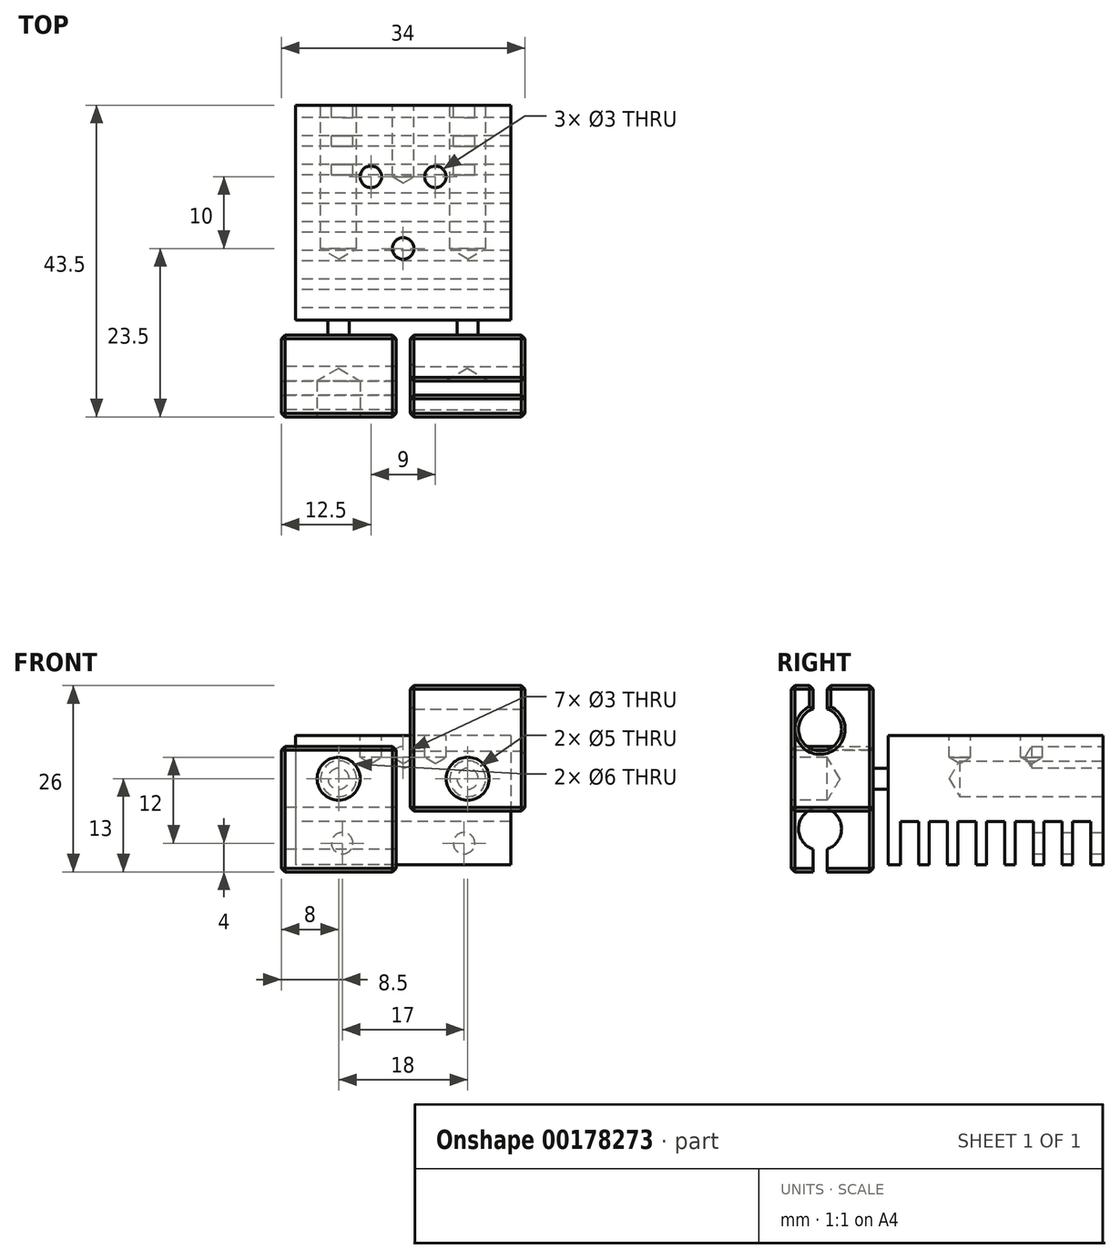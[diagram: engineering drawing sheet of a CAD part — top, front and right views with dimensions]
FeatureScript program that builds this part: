
annotation { "Feature Type Name" : "Feature", "Feature Type Description" : "" }
export const myFeature = defineFeature(function(context is Context, id is Id, definition is map)
    precondition{}
    {
        {
            var Q0;
            Q0=qCreatedBy(makeId("Top.planeOp"),FACE);
            var sketch = newSketch(context, id + "F0", { "sketchPlane" : qUnion([Q0])});
            skLineSegment(sketch, "E0.bottom", {"start": v(15, -15) * mm, "end": v(-15, -15) * mm});
            skLineSegment(sketch, "E0.top", {"start": v(15, 15) * mm, "end": v(-15, 15) * mm});
            skLineSegment(sketch, "E0.left", {"start": v(15, -15) * mm, "end": v(15, 15) * mm});
            skLineSegment(sketch, "E0.right", {"start": v(-15, -15) * mm, "end": v(-15, 15) * mm});
            skPoint(sketch, "E0.middle", {"position": v(0, 0) * mm});
            skSolve(sketch);
        }
        {
            var Q0;
            Q0=makeQuery(id+"F0.imprint","IMPRINT",FACE,{"disambiguationData":[TD([[makeQuery(id+"F0.imprint","IMPRINT",EDGE,{"derivedFrom":sQuery(id+"F0.wireOp",EDGE,"E0.bottom")}),-1.0]])]});
            extrude(context, id + "F10", {"entities" : qUnion([Q0]), "depth" : 18 * mm});
        }
        {
            var Q0;
            Q0=makeQuery(id+"F10.opExtrude","SWEPT_FACE",FACE,{"disambiguationData":[OSD([sQuery(id+"F0.wireOp",EDGE,"E0.top")])]});
            var sketch = newSketch(context, id + "F11", { "sketchPlane" : qUnion([Q0])});
            skPoint(sketch, "E1", {"position": v(-8.5, 3) * mm});
            skPoint(sketch, "E2", {"position": v(8.5, 3) * mm});
            skPoint(sketch, "E3", {"position": v(-9, 12) * mm});
            skPoint(sketch, "E4", {"position": v(9, 12) * mm});
            skPoint(sketch, "E5", {"position": v(0, 15) * mm});
            skSolve(sketch);
        }
        {
            var Q0;
            Q0=sQuery(id+"F11.wireOp",VERTEX,"E3");
            var Q1;
            Q1=sQuery(id+"F11.wireOp",VERTEX,"E4");
            var Q2;
            Q2=makeQuery(id+"F10.opExtrude","SWEPT_BODY",BODY,{"disambiguationData":[OSD([sQuery(id+"F0.wireOp",EDGE,"E0.bottom"),sQuery(id+"F0.wireOp",EDGE,"E0.top"),sQuery(id+"F0.wireOp",EDGE,"E0.left"),sQuery(id+"F0.wireOp",EDGE,"E0.right")])]});
            hole(context, id + "F1", {"style" : HoleStyle.SIMPLE, "endStyle" : HoleEndStyle.BLIND, "holeDiameter" : 5 * mm, "holeDepth" : 20 * mm, "locations" : qUnion([Q0, Q1]), "scope" : qUnion([Q2])});
        }
        {
            var Q0;
            Q0=makeQuery(id+"F10.opExtrude","CAP_FACE",FACE,{"disambiguationData":[OSD([sQuery(id+"F0.wireOp",EDGE,"E0.bottom"),sQuery(id+"F0.wireOp",EDGE,"E0.top"),sQuery(id+"F0.wireOp",EDGE,"E0.left"),sQuery(id+"F0.wireOp",EDGE,"E0.right")])],"isStart":true});
            var sketch = newSketch(context, id + "F12", { "sketchPlane" : qUnion([Q0])});
            skLineSegment(sketch, "E6.bottom", {"start": v(15, -13.25) * mm, "end": v(-15.01, -13.25) * mm});
            skLineSegment(sketch, "E6.top", {"start": v(15, -10.75) * mm, "end": v(-15.01, -10.75) * mm});
            skLineSegment(sketch, "E6.left", {"start": v(15, -13.25) * mm, "end": v(15, -10.75) * mm});
            skLineSegment(sketch, "E6.right", {"start": v(-15.01, -13.25) * mm, "end": v(-15.01, -10.75) * mm});
            skLineSegment(sketch, "E7.0.1.0", {"start": v(15, -9.25) * mm, "end": v(15, -6.75) * mm});
            skLineSegment(sketch, "E7.0.1.1", {"start": v(-15.01, -9.25) * mm, "end": v(-15.01, -6.75) * mm});
            skLineSegment(sketch, "E7.0.1.2", {"start": v(15, -9.25) * mm, "end": v(-15.01, -9.25) * mm});
            skLineSegment(sketch, "E7.0.1.3", {"start": v(15, -6.75) * mm, "end": v(-15.01, -6.75) * mm});
            skLineSegment(sketch, "E7.0.2.0", {"start": v(15, -5.25) * mm, "end": v(15, -2.75) * mm});
            skLineSegment(sketch, "E7.0.2.1", {"start": v(-15.01, -5.25) * mm, "end": v(-15.01, -2.75) * mm});
            skLineSegment(sketch, "E7.0.2.2", {"start": v(15, -5.25) * mm, "end": v(-15.01, -5.25) * mm});
            skLineSegment(sketch, "E7.0.2.3", {"start": v(15, -2.75) * mm, "end": v(-15.01, -2.75) * mm});
            skLineSegment(sketch, "E7.0.3.0", {"start": v(15, -1.25) * mm, "end": v(15, 1.25) * mm});
            skLineSegment(sketch, "E7.0.3.1", {"start": v(-15.01, -1.25) * mm, "end": v(-15.01, 1.25) * mm});
            skLineSegment(sketch, "E7.0.3.2", {"start": v(15, -1.25) * mm, "end": v(-15.01, -1.25) * mm});
            skLineSegment(sketch, "E7.0.3.3", {"start": v(15, 1.25) * mm, "end": v(-15.01, 1.25) * mm});
            skLineSegment(sketch, "E7.0.4.0", {"start": v(15, 2.75) * mm, "end": v(15, 5.25) * mm});
            skLineSegment(sketch, "E7.0.4.1", {"start": v(-15.01, 2.75) * mm, "end": v(-15.01, 5.25) * mm});
            skLineSegment(sketch, "E7.0.4.2", {"start": v(15, 2.75) * mm, "end": v(-15.01, 2.75) * mm});
            skLineSegment(sketch, "E7.0.4.3", {"start": v(15, 5.25) * mm, "end": v(-15.01, 5.25) * mm});
            skLineSegment(sketch, "E7.0.5.0", {"start": v(15, 6.75) * mm, "end": v(15, 9.25) * mm});
            skLineSegment(sketch, "E7.0.5.1", {"start": v(-15.01, 6.75) * mm, "end": v(-15.01, 9.25) * mm});
            skLineSegment(sketch, "E7.0.5.2", {"start": v(15, 6.75) * mm, "end": v(-15.01, 6.75) * mm});
            skLineSegment(sketch, "E7.0.5.3", {"start": v(15, 9.25) * mm, "end": v(-15.01, 9.25) * mm});
            skLineSegment(sketch, "E7.0.6.0", {"start": v(15, 10.75) * mm, "end": v(15, 13.25) * mm});
            skLineSegment(sketch, "E7.0.6.1", {"start": v(-15.01, 10.75) * mm, "end": v(-15.01, 13.25) * mm});
            skLineSegment(sketch, "E7.0.6.2", {"start": v(15, 10.75) * mm, "end": v(-15.01, 10.75) * mm});
            skLineSegment(sketch, "E7.0.6.3", {"start": v(15, 13.25) * mm, "end": v(-15.01, 13.25) * mm});
            skLineSegment(sketch, "E7.direction1", {"start": v(-15.01, -13.25) * mm, "end": v(9.99, -13.25) * mm, "construction": true});
            skLineSegment(sketch, "E7.direction2", {"start": v(-15.01, -13.25) * mm, "end": v(-15.01, -9.25) * mm, "construction": true});
            skSolve(sketch);
        }
        {
            var Q0;
            {var subQ0=sQuery(id+"F12.wireOp",EDGE,"E7.0.6.0");Q0=makeQuery(id+"F12.imprint","IMPRINT",FACE,{"disambiguationData":[TD([[makeQuery(id+"F12.imprint","IMPRINT",EDGE,{"derivedFrom":subQ0}),-1.0]])]});}
            var Q1;
            {var subQ0=sQuery(id+"F12.wireOp",EDGE,"E7.0.5.0");Q1=makeQuery(id+"F12.imprint","IMPRINT",FACE,{"disambiguationData":[TD([[makeQuery(id+"F12.imprint","IMPRINT",EDGE,{"derivedFrom":subQ0}),-1.0]])]});}
            var Q2;
            {var subQ0=sQuery(id+"F12.wireOp",EDGE,"E7.0.4.0");Q2=makeQuery(id+"F12.imprint","IMPRINT",FACE,{"disambiguationData":[TD([[makeQuery(id+"F12.imprint","IMPRINT",EDGE,{"derivedFrom":subQ0}),-1.0]])]});}
            var Q3;
            {var subQ0=sQuery(id+"F12.wireOp",EDGE,"E7.0.3.0");Q3=makeQuery(id+"F12.imprint","IMPRINT",FACE,{"disambiguationData":[TD([[makeQuery(id+"F12.imprint","IMPRINT",EDGE,{"derivedFrom":subQ0}),-1.0]])]});}
            var Q4;
            {var subQ0=sQuery(id+"F12.wireOp",EDGE,"E7.0.2.0");Q4=makeQuery(id+"F12.imprint","IMPRINT",FACE,{"disambiguationData":[TD([[makeQuery(id+"F12.imprint","IMPRINT",EDGE,{"derivedFrom":subQ0}),-1.0]])]});}
            var Q5;
            {var subQ0=sQuery(id+"F12.wireOp",EDGE,"E7.0.1.0");Q5=makeQuery(id+"F12.imprint","IMPRINT",FACE,{"disambiguationData":[TD([[makeQuery(id+"F12.imprint","IMPRINT",EDGE,{"derivedFrom":subQ0}),-1.0]])]});}
            var Q6;
            {var subQ0=sQuery(id+"F12.wireOp",EDGE,"E6.left");Q6=makeQuery(id+"F12.imprint","IMPRINT",FACE,{"disambiguationData":[TD([[makeQuery(id+"F12.imprint","IMPRINT",EDGE,{"derivedFrom":subQ0}),-1.0]])]});}
            extrude(context, id + "F13", {"entities" : qUnion([Q0, Q1, Q2, Q3, Q4, Q5, Q6]), "operationType" : NewBodyOperationType.REMOVE, "oppositeDirection" : true, "depth" : 6 * mm});
        }
        {
            var Q0;
            Q0=makeQuery(id+"F10.opExtrude","CAP_FACE",FACE,{"disambiguationData":[OSD([sQuery(id+"F0.wireOp",EDGE,"E0.bottom"),sQuery(id+"F0.wireOp",EDGE,"E0.top"),sQuery(id+"F0.wireOp",EDGE,"E0.left"),sQuery(id+"F0.wireOp",EDGE,"E0.right")])],"isStart":false});
            var sketch = newSketch(context, id + "F2", { "sketchPlane" : qUnion([Q0])});
            skPoint(sketch, "E8", {"position": v(-4.5, 5) * mm});
            skPoint(sketch, "E9", {"position": v(4.5, 5) * mm});
            skPoint(sketch, "E10", {"position": v(0, -5) * mm});
            skSolve(sketch);
        }
        {
            var Q0;
            Q0=sQuery(id+"F2.wireOp",VERTEX,"E9");
            var Q1;
            Q1=sQuery(id+"F2.wireOp",VERTEX,"E8");
            var Q2;
            Q2=sQuery(id+"F2.wireOp",VERTEX,"E10");
            var Q3;
            Q3=makeQuery(id+"F10.opExtrude","SWEPT_BODY",BODY,{"disambiguationData":[OSD([sQuery(id+"F0.wireOp",EDGE,"E0.bottom"),sQuery(id+"F0.wireOp",EDGE,"E0.top"),sQuery(id+"F0.wireOp",EDGE,"E0.left"),sQuery(id+"F0.wireOp",EDGE,"E0.right")])]});
            hole(context, id + "F14", {"style" : HoleStyle.SIMPLE, "endStyle" : HoleEndStyle.BLIND, "holeDiameter" : 3 * mm, "holeDepth" : 3 * mm, "locations" : qUnion([Q0, Q1, Q2]), "scope" : qUnion([Q3])});
        }
        {
            var Q0;
            Q0=sQuery(id+"F11.wireOp",VERTEX,"E2");
            var Q1;
            Q1=sQuery(id+"F11.wireOp",VERTEX,"E1");
            var Q2;
            Q2=sQuery(id+"F11.wireOp",VERTEX,"E5");
            var Q3;
            Q3=makeQuery(id+"F10.opExtrude","SWEPT_BODY",BODY,{"disambiguationData":[OSD([sQuery(id+"F0.wireOp",EDGE,"E0.bottom"),sQuery(id+"F0.wireOp",EDGE,"E0.top"),sQuery(id+"F0.wireOp",EDGE,"E0.left"),sQuery(id+"F0.wireOp",EDGE,"E0.right")])]});
            hole(context, id + "F15", {"style" : HoleStyle.SIMPLE, "endStyle" : HoleEndStyle.BLIND, "holeDiameter" : 3 * mm, "holeDepth" : 10 * mm, "locations" : qUnion([Q0, Q1, Q2]), "scope" : qUnion([Q3])});
        }
        {
            var Q0;
            Q0=makeQuery(id+"F10.opExtrude","SWEPT_FACE",FACE,{"disambiguationData":[OSD([sQuery(id+"F0.wireOp",EDGE,"E0.bottom")])]});
            var sketch = newSketch(context, id + "F3", { "sketchPlane" : qUnion([Q0])});
            skCircle(sketch, "E11", {"center": v(9, 12) * mm, "radius": 1.48 * mm});
            skCircle(sketch, "E12", {"center": v(-9, 12) * mm, "radius": 1.48 * mm});
            skSolve(sketch);
        }
        {
            var Q0;
            Q0=makeQuery(id+"F3.imprint","IMPRINT",FACE,{"disambiguationData":[TD([[makeQuery(id+"F3.imprint","IMPRINT",EDGE,{"derivedFrom":sQuery(id+"F3.wireOp",EDGE,"E12")}),1.0]])]});
            var Q1;
            Q1=makeQuery(id+"F3.imprint","IMPRINT",FACE,{"disambiguationData":[TD([[makeQuery(id+"F3.imprint","IMPRINT",EDGE,{"derivedFrom":sQuery(id+"F3.wireOp",EDGE,"E11")}),1.0]])]});
            extrude(context, id + "F4", {"entities" : qUnion([Q0, Q1]), "operationType" : NewBodyOperationType.ADD, "depth" : 2.1 * mm});
        }
        {
            var Q0;
            Q0=makeQuery(id+"F4.opExtrude","CAP_FACE",FACE,{"disambiguationData":[OSD([sQuery(id+"F3.wireOp",EDGE,"E11")])],"isStart":false});
            var sketch = newSketch(context, id + "F16", { "sketchPlane" : qUnion([Q0])});
            skLineSegment(sketch, "E13.bottom", {"start": v(1, 25) * mm, "end": v(17, 25) * mm});
            skLineSegment(sketch, "E13.top", {"start": v(1, 7.5) * mm, "end": v(17, 7.5) * mm});
            skLineSegment(sketch, "E13.left", {"start": v(1, 25) * mm, "end": v(1, 7.5) * mm});
            skLineSegment(sketch, "E13.right", {"start": v(17, 25) * mm, "end": v(17, 7.5) * mm});
            skPoint(sketch, "E14", {"position": v(9, 12) * mm});
            skSolve(sketch);
        }
        {
            var Q0;
            Q0=makeQuery(id+"F4.opExtrude","CAP_FACE",FACE,{"disambiguationData":[OSD([sQuery(id+"F3.wireOp",EDGE,"E12")])],"isStart":false});
            var sketch = newSketch(context, id + "F17", { "sketchPlane" : qUnion([Q0])});
            skPoint(sketch, "E15", {"position": v(-9, 12) * mm});
            skLineSegment(sketch, "E16.bottom", {"start": v(-17, 16.5) * mm, "end": v(-1, 16.5) * mm});
            skLineSegment(sketch, "E16.top", {"start": v(-17, -1) * mm, "end": v(-1, -1) * mm});
            skLineSegment(sketch, "E16.left", {"start": v(-17, 16.5) * mm, "end": v(-17, -1) * mm});
            skLineSegment(sketch, "E16.right", {"start": v(-1, 16.5) * mm, "end": v(-1, -1) * mm});
            skSolve(sketch);
        }
        {
            var Q0;
            Q0 = qSketchRegion(id + "F17", true);
            var Q1;
            Q1 = qSketchRegion(id + "F16", true);
            extrude(context, id + "F18", {"entities" : qUnion([Q0, Q1]), "operationType" : NewBodyOperationType.ADD, "depth" : 11.4 * mm});
        }
        {
            var Q0;
            Q0=makeQuery(id+"F18.opExtrude","CAP_FACE",FACE,{"disambiguationData":[OSD([sQuery(id+"F16.wireOp",EDGE,"E13.bottom"),sQuery(id+"F16.wireOp",EDGE,"E13.top"),sQuery(id+"F16.wireOp",EDGE,"E13.left"),sQuery(id+"F16.wireOp",EDGE,"E13.right")])],"isStart":false});
            var sketch = newSketch(context, id + "F19", { "sketchPlane" : qUnion([Q0])});
            skPoint(sketch, "E17", {"position": v(9, 12) * mm});
            skPoint(sketch, "E17.positionSnap0", {"position": v(9, 7.5) * mm});
            skSolve(sketch);
        }
        {
            var Q0;
            Q0=makeQuery(id+"F18.opExtrude","CAP_FACE",FACE,{"disambiguationData":[OSD([sQuery(id+"F17.wireOp",EDGE,"E16.bottom"),sQuery(id+"F17.wireOp",EDGE,"E16.top"),sQuery(id+"F17.wireOp",EDGE,"E16.left"),sQuery(id+"F17.wireOp",EDGE,"E16.right")])],"isStart":false});
            var sketch = newSketch(context, id + "F20", { "sketchPlane" : qUnion([Q0])});
            skPoint(sketch, "E18", {"position": v(-9, 12) * mm});
            skPoint(sketch, "E18.positionSnap0", {"position": v(-9, 16.5) * mm});
            skSolve(sketch);
        }
        {
            var Q0;
            Q0=sQuery(id+"F20.wireOp",VERTEX,"E18");
            var Q1;
            Q1=sQuery(id+"F19.wireOp",VERTEX,"E17");
            var Q2;
            Q2=makeQuery(id+"F10.opExtrude","SWEPT_BODY",BODY,{"disambiguationData":[OSD([sQuery(id+"F0.wireOp",EDGE,"E0.bottom"),sQuery(id+"F0.wireOp",EDGE,"E0.top"),sQuery(id+"F0.wireOp",EDGE,"E0.left"),sQuery(id+"F0.wireOp",EDGE,"E0.right")])]});
            hole(context, id + "F5", {"style" : HoleStyle.SIMPLE, "endStyle" : HoleEndStyle.BLIND, "holeDiameter" : 6 * mm, "holeDepth" : 5 * mm, "locations" : qUnion([Q0, Q1]), "scope" : qUnion([Q2])});
        }
        {
            var Q0;
            Q0=makeQuery(id+"F18.opExtrude","SWEPT_FACE",FACE,{"disambiguationData":[OSD([sQuery(id+"F16.wireOp",EDGE,"E13.right")])]});
            var sketch = newSketch(context, id + "F6", { "sketchPlane" : qUnion([Q0])});
            skArc(sketch, "E19", {"start": v(-25.5, 21.73) * mm, "mid": v(-24.5, 15.9) * mm, "end": v(-23.5, 21.73) * mm});
            skLineSegment(sketch, "E20.bottom", {"start": v(-25.5, 30.74) * mm, "end": v(-23.5, 30.74) * mm});
            skLineSegment(sketch, "E20.top", {"start": v(-25.5, 7.06) * mm, "end": v(-23.5, 7.06) * mm});
            skLineSegment(sketch, "E20.left", {"start": v(-25.5, 30.74) * mm, "end": v(-25.5, 21.73) * mm});
            skLineSegment(sketch, "E20.right", {"start": v(-23.5, 30.74) * mm, "end": v(-23.5, 21.73) * mm});
            skSolve(sketch);
        }
        {
            var Q0;
            {var subQ0=sQuery(id+"F6.wireOp",EDGE,"E19");Q0=makeQuery(id+"F6.imprint","IMPRINT",FACE,{"disambiguationData":[TD([[makeQuery(id+"F6.imprint","IMPRINT",EDGE,{"derivedFrom":subQ0}),1.0]])]});}
            extrude(context, id + "F7", {"entities" : qUnion([Q0]), "operationType" : NewBodyOperationType.REMOVE, "endBound" : BoundingType.UP_TO_NEXT, "oppositeDirection" : true, "depth" : 25 * mm});
        }
        {
            var Q0;
            Q0=makeQuery(id+"F18.opExtrude","SWEPT_FACE",FACE,{"disambiguationData":[OSD([sQuery(id+"F16.wireOp",EDGE,"E13.right")])]});
            var Q1;
            Q1=makeQuery(id+"F18.opExtrude","SWEPT_FACE",FACE,{"disambiguationData":[OSD([sQuery(id+"F16.wireOp",EDGE,"E13.top")])]});
            var Q2;
            Q2=makeQuery(id+"F18.opExtrude","SWEPT_FACE",FACE,{"disambiguationData":[OSD([sQuery(id+"F17.wireOp",EDGE,"E16.top")])]});
            var Q3;
            Q3=makeQuery(id+"F18.opExtrude","SWEPT_FACE",FACE,{"disambiguationData":[OSD([sQuery(id+"F17.wireOp",EDGE,"E16.right")])]});
            var Q4;
            {var subQ2=sQuery(id+"F16.wireOp",EDGE,"E13.bottom");Q4=makeQuery(id+"F7.boolean.opBoolean","SPLIT",FACE,{"disambiguationData":[TD([makeQuery(id+"F7.opExtrude","SWEPT_FACE",FACE,{"disambiguationData":[OSD([sQuery(id+"F6.wireOp",EDGE,"E20.right")])]})])],"derivedFrom":makeQuery(id+"F18.opExtrude","SWEPT_FACE",FACE,{"disambiguationData":[OSD([subQ2])]})});}
            var Q5;
            {var subQ2=sQuery(id+"F16.wireOp",EDGE,"E13.bottom");Q5=makeQuery(id+"F7.boolean.opBoolean","SPLIT",FACE,{"disambiguationData":[TD([makeQuery(id+"F7.opExtrude","SWEPT_FACE",FACE,{"disambiguationData":[OSD([sQuery(id+"F6.wireOp",EDGE,"E20.left")])]})])],"derivedFrom":makeQuery(id+"F18.opExtrude","SWEPT_FACE",FACE,{"disambiguationData":[OSD([subQ2])]})});}
            var Q6;
            Q6=makeQuery(id+"F18.opExtrude","SWEPT_FACE",FACE,{"disambiguationData":[OSD([sQuery(id+"F17.wireOp",EDGE,"E16.bottom")])]});
            var Q7;
            Q7=makeQuery(id+"F18.opExtrude","SWEPT_FACE",FACE,{"disambiguationData":[OSD([sQuery(id+"F17.wireOp",EDGE,"E16.left")])]});
            var Q8;
            Q8=makeQuery(id+"F18.opExtrude","SWEPT_FACE",FACE,{"disambiguationData":[OSD([sQuery(id+"F16.wireOp",EDGE,"E13.left")])]});
            chamfer(context, id + "F8", {"entities" : qUnion([Q0, Q1, Q2, Q3, Q4, Q5, Q6, Q7, Q8]), "width" : 0.5 * mm, "tangentPropagation" : true});
        }
        {
            var Q0;
            Q0=makeQuery(id+"F18.opExtrude","SWEPT_FACE",FACE,{"disambiguationData":[OSD([sQuery(id+"F17.wireOp",EDGE,"E16.left")])]});
            var sketch = newSketch(context, id + "F9", { "sketchPlane" : qUnion([Q0])});
            skArc(sketch, "E21", {"start": v(25.5, 2.17) * mm, "mid": v(24.5, 8) * mm, "end": v(23.5, 2.17) * mm});
            skLineSegment(sketch, "E22.top", {"start": v(25.5, -1.5) * mm, "end": v(23.5, -1.5) * mm});
            skLineSegment(sketch, "E22.left", {"start": v(25.5, 11.5) * mm, "end": v(25.5, 7.83) * mm});
            skLineSegment(sketch, "E22.right", {"start": v(23.5, 2.17) * mm, "end": v(23.5, -1.5) * mm});
            skPoint(sketch, "E23.orphan", {"position": v(23.5, 11.5) * mm});
            skLineSegment(sketch, "E24.trimOffspring", {"start": v(25.5, 2.17) * mm, "end": v(25.5, -1.5) * mm});
            skSolve(sketch);
        }
        {
            var Q0;
            {var subQ1=sQuery(id+"F9.wireOp",EDGE,"E21");var subQ9=makeQuery(id+"F9.imprint","IMPRINT",VERTEX,{"derivedFrom":subQ1});Q0=makeQuery(id+"F9.imprint","IMPRINT",FACE,{"disambiguationData":[TD([[makeQuery(id+"F9.imprint","IMPRINT",EDGE,{"disambiguationData":[TD([[subQ9,1.0]])],"derivedFrom":subQ1}),1.0]])]});}
            var Q1;
            {var subQ0=sQuery(id+"F9.wireOp",EDGE,"E22.top");Q1=makeQuery(id+"F9.imprint","IMPRINT",FACE,{"disambiguationData":[TD([[makeQuery(id+"F9.imprint","IMPRINT",EDGE,{"derivedFrom":subQ0}),-1.0]])]});}
            extrude(context, id + "F21", {"entities" : qUnion([Q0, Q1]), "operationType" : NewBodyOperationType.REMOVE, "endBound" : BoundingType.UP_TO_NEXT, "oppositeDirection" : true, "depth" : 25 * mm});
        }
    });
